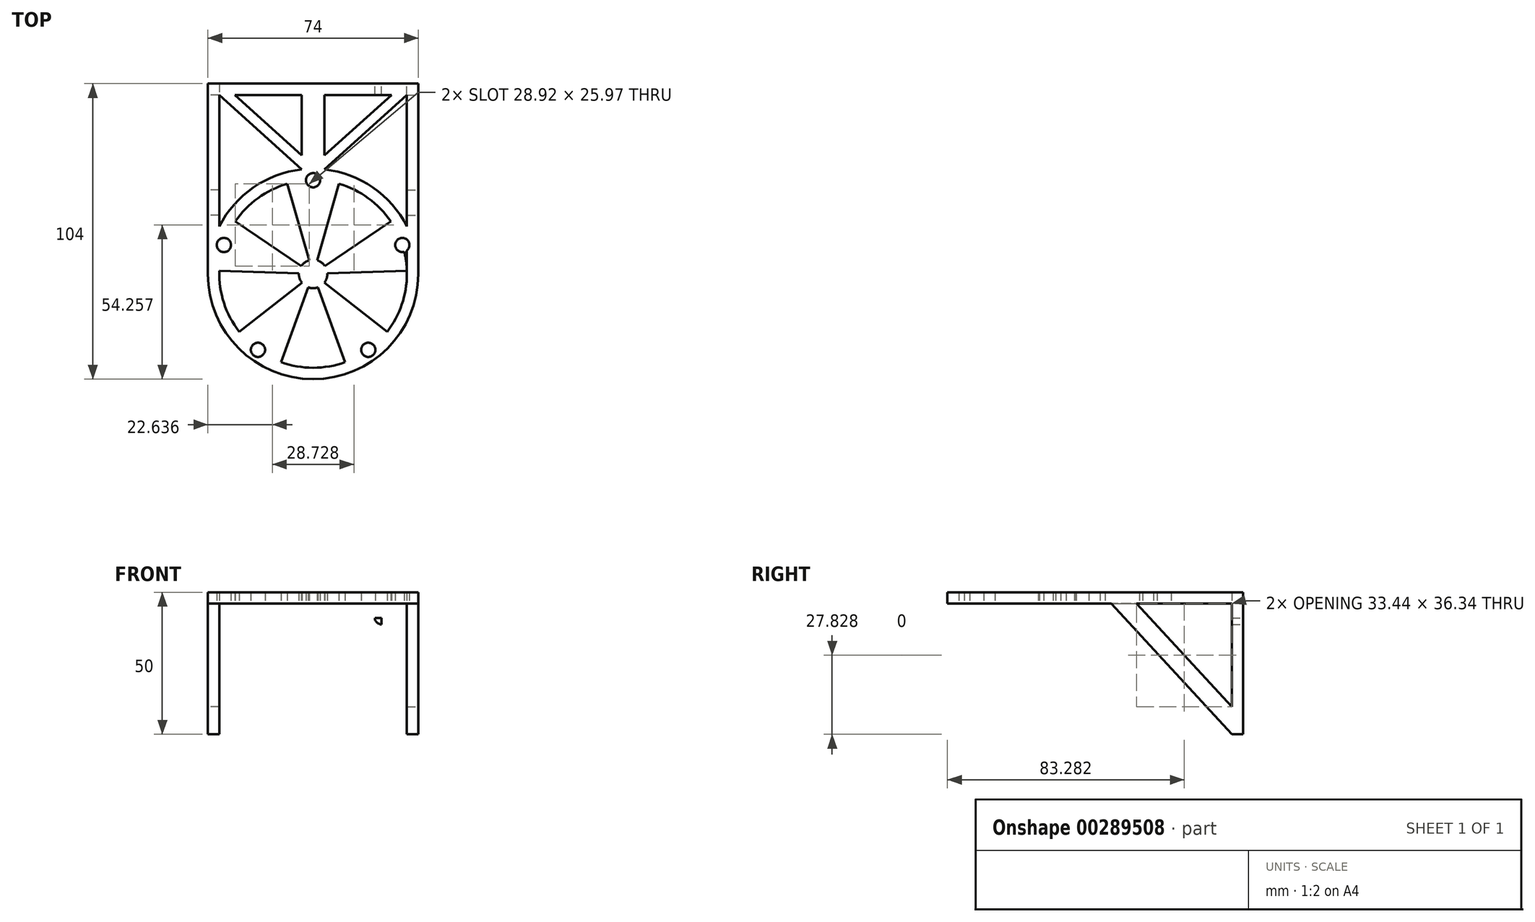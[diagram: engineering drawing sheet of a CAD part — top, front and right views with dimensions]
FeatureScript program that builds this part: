
annotation { "Feature Type Name" : "Feature", "Feature Type Description" : "" }
export const myFeature = defineFeature(function(context is Context, id is Id, definition is map)
    precondition{}
    {
        {
            var Q0;
            Q0=qCreatedBy(makeId("Top.planeOp"),FACE);
            var sketch = newSketch(context, id + "F0", { "sketchPlane" : qUnion([Q0])});
            skCircle(sketch, "E0", {"center": v(0, 33) * mm, "radius": 2.5 * mm});
            skCircle(sketch, "E1.1.0", {"center": v(-31.38, 10.2) * mm, "radius": 2.5 * mm});
            skCircle(sketch, "E1.2.0", {"center": v(-19.4, -26.7) * mm, "radius": 2.5 * mm});
            skCircle(sketch, "E1.3.0", {"center": v(19.4, -26.7) * mm, "radius": 2.5 * mm});
            skCircle(sketch, "E1.4.0", {"center": v(31.38, 10.2) * mm, "radius": 2.5 * mm});
            skPoint(sketch, "E1.center", {"position": v(0, 0) * mm});
            skLineSegment(sketch, "E2", {"start": v(0, 67) * mm, "end": v(37, 67) * mm});
            skLineSegment(sketch, "E3", {"start": v(37, 67) * mm, "end": v(-37, 67) * mm});
            skLineSegment(sketch, "E4", {"start": v(-37, 67) * mm, "end": v(-37, 0) * mm});
            skLineSegment(sketch, "E5", {"start": v(37, 67) * mm, "end": v(37, 0) * mm});
            skLineSegment(sketch, "E6", {"start": v(23.54, 15.9) * mm, "end": v(0, 0) * mm});
            skLineSegment(sketch, "E7", {"start": v(23.54, 15.9) * mm, "end": v(27.35, 18.47) * mm});
            skLineSegment(sketch, "E8", {"start": v(7.85, 27.3) * mm, "end": v(0, 0) * mm});
            skLineSegment(sketch, "E9", {"start": v(0, 0) * mm, "end": v(9.12, 31.72) * mm});
            skLineSegment(sketch, "E10.1.0", {"start": v(0, 0) * mm, "end": v(-27.35, 18.47) * mm});
            skLineSegment(sketch, "E10.1.2", {"start": v(-7.85, 27.3) * mm, "end": v(0, 0) * mm});
            skLineSegment(sketch, "E10.1.4", {"start": v(-7.85, 27.3) * mm, "end": v(-9.12, 31.72) * mm});
            skLineSegment(sketch, "E10.2.0", {"start": v(0, 0) * mm, "end": v(-26.02, -20.3) * mm});
            skLineSegment(sketch, "E10.2.2", {"start": v(-28.39, 0.97) * mm, "end": v(0, 0) * mm});
            skLineSegment(sketch, "E10.2.4", {"start": v(-28.39, 0.97) * mm, "end": v(-32.98, 1.13) * mm});
            skLineSegment(sketch, "E10.3.0", {"start": v(0, 0) * mm, "end": v(11.27, -31.02) * mm});
            skLineSegment(sketch, "E10.3.2", {"start": v(-9.7, -26.7) * mm, "end": v(0, 0) * mm});
            skLineSegment(sketch, "E10.3.4", {"start": v(-9.7, -26.7) * mm, "end": v(-11.27, -31.02) * mm});
            skLineSegment(sketch, "E10.4.0", {"start": v(0, 0) * mm, "end": v(32.98, 1.13) * mm});
            skLineSegment(sketch, "E10.4.2", {"start": v(22.4, -17.47) * mm, "end": v(0, 0) * mm});
            skLineSegment(sketch, "E10.4.4", {"start": v(22.4, -17.47) * mm, "end": v(26.02, -20.3) * mm});
            skLineSegment(sketch, "E11.0", {"start": v(-33, 63) * mm, "end": v(-33, 0) * mm});
            skLineSegment(sketch, "E11.1", {"start": v(33, 63) * mm, "end": v(-33, 63) * mm});
            skLineSegment(sketch, "E11.2", {"start": v(33, 63) * mm, "end": v(33, 0) * mm});
            skLineSegment(sketch, "E12", {"start": v(0, 63) * mm, "end": v(4, 63) * mm});
            skLineSegment(sketch, "E13", {"start": v(4, 63) * mm, "end": v(0, 63) * mm});
            skLineSegment(sketch, "E14.bottom", {"start": v(4, 63) * mm, "end": v(-4, 63) * mm});
            skCircle(sketch, "E15", {"center": v(0, 0) * mm, "radius": 37 * mm});
            skCircle(sketch, "E16", {"center": v(0, 0) * mm, "radius": 33 * mm});
            skCircle(sketch, "E17", {"center": v(0, 0) * mm, "radius": 5 * mm});
            skLineSegment(sketch, "E18", {"start": v(4, 63) * mm, "end": v(4, 36.78) * mm});
            skLineSegment(sketch, "E19", {"start": v(-4, 63) * mm, "end": v(-4, 36.78) * mm});
            skLineSegment(sketch, "E20", {"start": v(-4, 36.78) * mm, "end": v(-33, 63) * mm});
            skLineSegment(sketch, "E21", {"start": v(4, 36.78) * mm, "end": v(33, 63) * mm});
            skLineSegment(sketch, "E22", {"start": v(4, 41.7) * mm, "end": v(27.56, 63) * mm});
            skLineSegment(sketch, "E23", {"start": v(4, 41.7) * mm, "end": v(-4, 41.7) * mm});
            skLineSegment(sketch, "E24", {"start": v(-4, 41.7) * mm, "end": v(-27.56, 63) * mm});
            skSolve(sketch);
        }
        {
            var Q0;
            Q0 = qSketchRegion(id + "F0", true);
            var Q1;
            {var subQ4=sQuery(id+"F0.wireOp",EDGE,"E23");Q1=makeQuery(id+"F0.imprint","IMPRINT",FACE,{"disambiguationData":[TD([[makeQuery(id+"F0.imprint","IMPRINT",EDGE,{"derivedFrom":subQ4}),-1.0]])]});}
            var Q2;
            {var subQ5=sQuery(id+"F0.wireOp",EDGE,"E23");Q2=makeQuery(id+"F0.imprint","IMPRINT",FACE,{"disambiguationData":[TD([[makeQuery(id+"F0.imprint","IMPRINT",EDGE,{"derivedFrom":subQ5}),1.0]])]});}
            var Q3;
            {var subQ0=sQuery(id+"F0.wireOp",EDGE,"E21");Q3=makeQuery(id+"F0.imprint","IMPRINT",FACE,{"disambiguationData":[TD([[makeQuery(id+"F0.imprint","IMPRINT",EDGE,{"derivedFrom":subQ0}),1.0]])]});}
            var Q4;
            {var subQ0=sQuery(id+"F0.wireOp",EDGE,"E20");Q4=makeQuery(id+"F0.imprint","IMPRINT",FACE,{"disambiguationData":[TD([[makeQuery(id+"F0.imprint","IMPRINT",EDGE,{"derivedFrom":subQ0}),-1.0]])]});}
            var Q5;
            {var subQ7=sQuery(id+"F0.wireOp",EDGE,"E16");var subQ14=sQuery(id+"F0.wireOp",EDGE,"E0");var subQ15=makeQuery(id+"F0.imprint","INTERSECT",VERTEX,{"disambiguationData":[OD(0.0)],"derivedFrom":[subQ14,subQ7]});Q5=makeQuery(id+"F0.imprint","IMPRINT",FACE,{"disambiguationData":[TD([[makeQuery(id+"F0.imprint","IMPRINT",EDGE,{"disambiguationData":[TD([[subQ15,-1.0]])],"derivedFrom":subQ14}),-1.0]])]});}
            var Q6;
            {var subQ11=sQuery(id+"F0.wireOp",EDGE,"E10.1.4");Q6=makeQuery(id+"F0.imprint","IMPRINT",FACE,{"disambiguationData":[TD([[makeQuery(id+"F0.imprint","IMPRINT",EDGE,{"derivedFrom":subQ11}),-1.0]])]});}
            var Q7;
            {var subQ5=sQuery(id+"F0.wireOp",EDGE,"E7");Q7=makeQuery(id+"F0.imprint","IMPRINT",FACE,{"disambiguationData":[TD([[makeQuery(id+"F0.imprint","IMPRINT",EDGE,{"derivedFrom":subQ5}),-1.0]])]});}
            var Q8;
            {var subQ0=sQuery(id+"F0.wireOp",EDGE,"E10.4.4");Q8=makeQuery(id+"F0.imprint","IMPRINT",FACE,{"disambiguationData":[TD([[makeQuery(id+"F0.imprint","IMPRINT",EDGE,{"derivedFrom":subQ0}),-1.0]])]});}
            var Q9;
            {var subQ0=sQuery(id+"F0.wireOp",EDGE,"E10.3.4");Q9=makeQuery(id+"F0.imprint","IMPRINT",FACE,{"disambiguationData":[TD([[makeQuery(id+"F0.imprint","IMPRINT",EDGE,{"derivedFrom":subQ0}),-1.0]])]});}
            var Q10;
            {var subQ1=sQuery(id+"F0.wireOp",EDGE,"E10.1.0");var subQ3=sQuery(id+"F0.wireOp",EDGE,"E17");var subQ4=makeQuery(id+"F0.imprint","INTERSECT",VERTEX,{"derivedFrom":[subQ1,subQ3]});Q10=makeQuery(id+"F0.imprint","IMPRINT",FACE,{"disambiguationData":[TD([[makeQuery(id+"F0.imprint","IMPRINT",EDGE,{"disambiguationData":[TD([[subQ4,-1.0]])],"derivedFrom":subQ3}),1.0]])]});}
            var Q11;
            {var subQ0=sQuery(id+"F0.wireOp",EDGE,"E10.2.4");Q11=makeQuery(id+"F0.imprint","IMPRINT",FACE,{"disambiguationData":[TD([[makeQuery(id+"F0.imprint","IMPRINT",EDGE,{"derivedFrom":subQ0}),-1.0]])]});}
            var Q12;
            {var subQ1=sQuery(id+"F0.wireOp",EDGE,"E10.2.0");var subQ3=sQuery(id+"F0.wireOp",EDGE,"E17");var subQ4=makeQuery(id+"F0.imprint","INTERSECT",VERTEX,{"derivedFrom":[subQ1,subQ3]});Q12=makeQuery(id+"F0.imprint","IMPRINT",FACE,{"disambiguationData":[TD([[makeQuery(id+"F0.imprint","IMPRINT",EDGE,{"disambiguationData":[TD([[subQ4,1.0]])],"derivedFrom":subQ3}),1.0]])]});}
            var Q13;
            {var subQ1=sQuery(id+"F0.wireOp",EDGE,"E10.2.0");var subQ3=sQuery(id+"F0.wireOp",EDGE,"E17");var subQ4=makeQuery(id+"F0.imprint","INTERSECT",VERTEX,{"derivedFrom":[subQ1,subQ3]});Q13=makeQuery(id+"F0.imprint","IMPRINT",FACE,{"disambiguationData":[TD([[makeQuery(id+"F0.imprint","IMPRINT",EDGE,{"disambiguationData":[TD([[subQ4,-1.0]])],"derivedFrom":subQ3}),1.0]])]});}
            var Q14;
            {var subQ1=sQuery(id+"F0.wireOp",EDGE,"E10.3.0");var subQ3=sQuery(id+"F0.wireOp",EDGE,"E17");var subQ4=makeQuery(id+"F0.imprint","INTERSECT",VERTEX,{"derivedFrom":[subQ1,subQ3]});Q14=makeQuery(id+"F0.imprint","IMPRINT",FACE,{"disambiguationData":[TD([[makeQuery(id+"F0.imprint","IMPRINT",EDGE,{"disambiguationData":[TD([[subQ4,1.0]])],"derivedFrom":subQ3}),1.0]])]});}
            var Q15;
            {var subQ1=sQuery(id+"F0.wireOp",EDGE,"E10.3.0");var subQ3=sQuery(id+"F0.wireOp",EDGE,"E17");var subQ4=makeQuery(id+"F0.imprint","INTERSECT",VERTEX,{"derivedFrom":[subQ1,subQ3]});Q15=makeQuery(id+"F0.imprint","IMPRINT",FACE,{"disambiguationData":[TD([[makeQuery(id+"F0.imprint","IMPRINT",EDGE,{"disambiguationData":[TD([[subQ4,-1.0]])],"derivedFrom":subQ3}),1.0]])]});}
            var Q16;
            {var subQ1=sQuery(id+"F0.wireOp",EDGE,"E10.4.0");var subQ3=sQuery(id+"F0.wireOp",EDGE,"E17");var subQ4=makeQuery(id+"F0.imprint","INTERSECT",VERTEX,{"derivedFrom":[subQ1,subQ3]});Q16=makeQuery(id+"F0.imprint","IMPRINT",FACE,{"disambiguationData":[TD([[makeQuery(id+"F0.imprint","IMPRINT",EDGE,{"disambiguationData":[TD([[subQ4,1.0]])],"derivedFrom":subQ3}),1.0]])]});}
            var Q17;
            {var subQ1=sQuery(id+"F0.wireOp",EDGE,"E6");var subQ3=sQuery(id+"F0.wireOp",EDGE,"E17");var subQ4=makeQuery(id+"F0.imprint","INTERSECT",VERTEX,{"derivedFrom":[subQ1,subQ3]});Q17=makeQuery(id+"F0.imprint","IMPRINT",FACE,{"disambiguationData":[TD([[makeQuery(id+"F0.imprint","IMPRINT",EDGE,{"disambiguationData":[TD([[subQ4,1.0]])],"derivedFrom":subQ3}),1.0]])]});}
            var Q18;
            {var subQ1=sQuery(id+"F0.wireOp",EDGE,"E6");var subQ3=sQuery(id+"F0.wireOp",EDGE,"E17");var subQ4=makeQuery(id+"F0.imprint","INTERSECT",VERTEX,{"derivedFrom":[subQ1,subQ3]});Q18=makeQuery(id+"F0.imprint","IMPRINT",FACE,{"disambiguationData":[TD([[makeQuery(id+"F0.imprint","IMPRINT",EDGE,{"disambiguationData":[TD([[subQ4,-1.0]])],"derivedFrom":subQ3}),1.0]])]});}
            var Q19;
            {var subQ1=sQuery(id+"F0.wireOp",EDGE,"E9");var subQ3=sQuery(id+"F0.wireOp",EDGE,"E17");var subQ4=makeQuery(id+"F0.imprint","INTERSECT",VERTEX,{"derivedFrom":[subQ1,subQ3]});Q19=makeQuery(id+"F0.imprint","IMPRINT",FACE,{"disambiguationData":[TD([[makeQuery(id+"F0.imprint","IMPRINT",EDGE,{"disambiguationData":[TD([[subQ4,-1.0]])],"derivedFrom":subQ3}),1.0]])]});}
            var Q20;
            {var subQ1=sQuery(id+"F0.wireOp",EDGE,"E10.1.0");var subQ3=sQuery(id+"F0.wireOp",EDGE,"E17");var subQ4=makeQuery(id+"F0.imprint","INTERSECT",VERTEX,{"derivedFrom":[subQ1,subQ3]});Q20=makeQuery(id+"F0.imprint","IMPRINT",FACE,{"disambiguationData":[TD([[makeQuery(id+"F0.imprint","IMPRINT",EDGE,{"disambiguationData":[TD([[subQ4,1.0]])],"derivedFrom":subQ3}),1.0]])]});}
            var Q21;
            {var subQ0=sQuery(id+"F0.wireOp",EDGE,"E11.0");var subQ1=sQuery(id+"F0.wireOp",EDGE,"E1.1.0");var subQ2=makeQuery(id+"F0.imprint","INTERSECT",VERTEX,{"disambiguationData":[OD(0.0)],"derivedFrom":[subQ1,subQ0]});Q21=makeQuery(id+"F0.imprint","IMPRINT",FACE,{"disambiguationData":[TD([[makeQuery(id+"F0.imprint","IMPRINT",EDGE,{"disambiguationData":[TD([[subQ2,-1.0]])],"derivedFrom":subQ1}),-1.0]])]});}
            var Q22;
            {var subQ0=sQuery(id+"F0.wireOp",EDGE,"E11.2");var subQ1=sQuery(id+"F0.wireOp",EDGE,"E1.4.0");var subQ2=makeQuery(id+"F0.imprint","INTERSECT",VERTEX,{"disambiguationData":[OD(1.0)],"derivedFrom":[subQ1,subQ0]});Q22=makeQuery(id+"F0.imprint","IMPRINT",FACE,{"disambiguationData":[TD([[makeQuery(id+"F0.imprint","IMPRINT",EDGE,{"disambiguationData":[TD([[subQ2,1.0]])],"derivedFrom":subQ1}),-1.0]])]});}
            extrude(context, id + "F1", {"entities" : qUnion([Q0, Q1, Q2, Q3, Q4, Q5, Q6, Q7, Q8, Q9, Q10, Q11, Q12, Q13, Q14, Q15, Q16, Q17, Q18, Q19, Q20, Q21, Q22]), "depth" : 4 * mm});
        }
        {
            var Q0;
            Q0=makeQuery(id+"F1.opExtrude","SWEPT_FACE",FACE,{"disambiguationData":[OSD([sQuery(id+"F0.wireOp",EDGE,"E4")])]});
            var sketch = newSketch(context, id + "F2", { "sketchPlane" : qUnion([Q0])});
            skLineSegment(sketch, "E25.bottom", {"start": v(-67, 4) * mm, "end": v(-17, 4) * mm});
            skLineSegment(sketch, "E25.top", {"start": v(-67, -46) * mm, "end": v(-17, -46) * mm});
            skLineSegment(sketch, "E25.left", {"start": v(-67, 4) * mm, "end": v(-67, -46) * mm});
            skLineSegment(sketch, "E25.right", {"start": v(-17, 4) * mm, "end": v(-17, -46) * mm});
            skLineSegment(sketch, "E26.0", {"start": v(-63, 0) * mm, "end": v(-29.56, 0) * mm});
            skLineSegment(sketch, "E26.1", {"start": v(-63, 0) * mm, "end": v(-63, -36.34) * mm});
            skLineSegment(sketch, "E26.2", {"start": v(-63, -36.34) * mm, "end": v(-29.56, 0) * mm});
            skLineSegment(sketch, "E27", {"start": v(-63, -36.34) * mm, "end": v(-63, -46) * mm});
            skLineSegment(sketch, "E28", {"start": v(-63, -46) * mm, "end": v(-17, 4) * mm});
            skSolve(sketch);
        }
        {
            var Q0;
            {var subQ1=sQuery(id+"F2.wireOp",EDGE,"E25.right");var subQ2=sQuery(id+"F0.wireOp",EDGE,"E4");var subQ4=makeQuery(id+"F1.opExtrude","CAP_EDGE",EDGE,{"disambiguationData":[OSD([subQ2])],"isStart":true});var subQ5=makeQuery(id+"F2.imprint","INTERSECT",VERTEX,{"derivedFrom":[subQ4,subQ1]});Q0=makeQuery(id+"F2.imprint","IMPRINT",FACE,{"disambiguationData":[TD([[makeQuery(id+"F2.imprint","IMPRINT",EDGE,{"disambiguationData":[TD([[subQ5,1.0]])],"derivedFrom":subQ4}),1.0]])]});}
            var Q1;
            {var subQ1=sQuery(id+"F2.wireOp",EDGE,"E25.bottom");Q1=makeQuery(id+"F2.imprint","IMPRINT",FACE,{"disambiguationData":[TD([[makeQuery(id+"F2.imprint","IMPRINT",EDGE,{"derivedFrom":subQ1}),-1.0]])]});}
            var Q2;
            {var subQ1=sQuery(id+"F2.wireOp",EDGE,"E26.1");Q2=makeQuery(id+"F2.imprint","IMPRINT",FACE,{"disambiguationData":[TD([[makeQuery(id+"F2.imprint","IMPRINT",EDGE,{"derivedFrom":subQ1}),-1.0]])]});}
            var Q3;
            {var subQ0=sQuery(id+"F2.wireOp",EDGE,"E26.2");Q3=makeQuery(id+"F2.imprint","IMPRINT",FACE,{"disambiguationData":[TD([[makeQuery(id+"F2.imprint","IMPRINT",EDGE,{"derivedFrom":subQ0}),-1.0]])]});}
            extrude(context, id + "F3", {"entities" : qUnion([Q0, Q1, Q2, Q3]), "operationType" : NewBodyOperationType.ADD, "oppositeDirection" : true, "depth" : 4 * mm});
        }
        {
            var Q0;
            Q0=makeQuery(id+"F1.opExtrude","SWEPT_FACE",FACE,{"disambiguationData":[OSD([sQuery(id+"F0.wireOp",EDGE,"E5")])]});
            var sketch = newSketch(context, id + "F4", { "sketchPlane" : qUnion([Q0])});
            skLineSegment(sketch, "E29.bottom", {"start": v(67, 4) * mm, "end": v(17, 4) * mm});
            skLineSegment(sketch, "E29.top", {"start": v(67, -46) * mm, "end": v(17, -46) * mm});
            skLineSegment(sketch, "E29.left", {"start": v(67, 4) * mm, "end": v(67, -46) * mm});
            skLineSegment(sketch, "E29.right", {"start": v(17, 4) * mm, "end": v(17, -46) * mm});
            skLineSegment(sketch, "E30.0", {"start": v(63, 0) * mm, "end": v(26.66, 0) * mm});
            skLineSegment(sketch, "E30.1", {"start": v(63, 0) * mm, "end": v(63, -36.34) * mm});
            skLineSegment(sketch, "E31", {"start": v(63, -46) * mm, "end": v(17, 4) * mm});
            skLineSegment(sketch, "E32", {"start": v(63, -36.34) * mm, "end": v(29.56, 0) * mm});
            skSolve(sketch);
        }
        {
            var Q0;
            {var subQ1=sQuery(id+"F4.wireOp",EDGE,"E29.right");var subQ2=sQuery(id+"F0.wireOp",EDGE,"E5");var subQ4=makeQuery(id+"F1.opExtrude","CAP_EDGE",EDGE,{"disambiguationData":[OSD([subQ2])],"isStart":true});var subQ5=makeQuery(id+"F4.imprint","INTERSECT",VERTEX,{"derivedFrom":[subQ4,subQ1]});Q0=makeQuery(id+"F4.imprint","IMPRINT",FACE,{"disambiguationData":[TD([[makeQuery(id+"F4.imprint","IMPRINT",EDGE,{"disambiguationData":[TD([[subQ5,1.0]])],"derivedFrom":subQ4}),-1.0]])]});}
            var Q1;
            {var subQ1=sQuery(id+"F4.wireOp",EDGE,"E29.bottom");Q1=makeQuery(id+"F4.imprint","IMPRINT",FACE,{"disambiguationData":[TD([[makeQuery(id+"F4.imprint","IMPRINT",EDGE,{"derivedFrom":subQ1}),1.0]])]});}
            var Q2;
            {var subQ1=sQuery(id+"F4.wireOp",EDGE,"E30.1");Q2=makeQuery(id+"F4.imprint","IMPRINT",FACE,{"disambiguationData":[TD([[makeQuery(id+"F4.imprint","IMPRINT",EDGE,{"derivedFrom":subQ1}),1.0]])]});}
            extrude(context, id + "F5", {"entities" : qUnion([Q0, Q1, Q2]), "operationType" : NewBodyOperationType.ADD, "oppositeDirection" : true, "depth" : 4 * mm});
        }
        {
            var Q0;
            Q0=makeQuery(id+"F5.boolean.opBoolean","MERGE",FACE,{"derivedFrom":[makeQuery(id+"F3.boolean.opBoolean","MERGE",FACE,{"derivedFrom":[makeQuery(id+"F1.opExtrude","SWEPT_FACE",FACE,{"disambiguationData":[OSD([sQuery(id+"F0.wireOp",EDGE,"E3")])]}),makeQuery(id+"F3.opExtrude","SWEPT_FACE",FACE,{"disambiguationData":[OSD([sQuery(id+"F2.wireOp",EDGE,"E25.left")])]})]}),makeQuery(id+"F5.opExtrude","SWEPT_FACE",FACE,{"disambiguationData":[OSD([sQuery(id+"F4.wireOp",EDGE,"E29.left")])]})]});
            var sketch = newSketch(context, id + "F6", { "sketchPlane" : qUnion([Q0])});
            skLineSegment(sketch, "E33.bottom", {"start": v(-37, -46) * mm, "end": v(37, -46) * mm});
            skLineSegment(sketch, "E33.top", {"start": v(-37, -36) * mm, "end": v(37, -36) * mm});
            skLineSegment(sketch, "E33.left", {"start": v(-37, -46) * mm, "end": v(-37, -36) * mm});
            skLineSegment(sketch, "E33.right", {"start": v(37, -46) * mm, "end": v(37, -36) * mm});
            skLineSegment(sketch, "E34", {"start": v(-37, -36) * mm, "end": v(-37, 0) * mm});
            skLineSegment(sketch, "E35.bottom", {"start": v(-37, 0) * mm, "end": v(37, 0) * mm});
            skLineSegment(sketch, "E35.top", {"start": v(-37, -10) * mm, "end": v(37, -10) * mm});
            skLineSegment(sketch, "E35.left", {"start": v(-37, 0) * mm, "end": v(-37, -10) * mm});
            skLineSegment(sketch, "E35.right", {"start": v(37, 0) * mm, "end": v(37, -10) * mm});
            skLineSegment(sketch, "E36", {"start": v(0, 0) * mm, "end": v(0, -46) * mm});
            skLineSegment(sketch, "E37.bottom", {"start": v(0, 0) * mm, "end": v(0, 0) * mm});
            skLineSegment(sketch, "E37.top", {"start": v(0, -10) * mm, "end": v(0, -10) * mm});
            skLineSegment(sketch, "E37.left", {"start": v(0, 0) * mm, "end": v(0, -10) * mm});
            skLineSegment(sketch, "E37.right", {"start": v(0, 0) * mm, "end": v(0, -10) * mm});
            skPoint(sketch, "E38.oppositeSnap0", {"position": v(0, -5) * mm});
            skLineSegment(sketch, "E38.bottom", {"start": v(0, -5) * mm, "end": v(24, -5) * mm});
            skLineSegment(sketch, "E38.top", {"start": v(0, -5) * mm, "end": v(24, -5) * mm});
            skLineSegment(sketch, "E38.left", {"start": v(0, -5) * mm, "end": v(0, -5) * mm});
            skLineSegment(sketch, "E38.right", {"start": v(24, -5) * mm, "end": v(24, -5) * mm});
            skLineSegment(sketch, "E39", {"start": v(0, -46) * mm, "end": v(0, -36) * mm});
            skLineSegment(sketch, "E40", {"start": v(0, -36) * mm, "end": v(0, -41) * mm});
            skLineSegment(sketch, "E41", {"start": v(0, -41) * mm, "end": v(-24, -41) * mm});
            skLineSegment(sketch, "E42.bottom", {"start": v(24, -5) * mm, "end": v(-24, -5) * mm});
            skLineSegment(sketch, "E42.top", {"start": v(24, -41) * mm, "end": v(-24, -41) * mm});
            skLineSegment(sketch, "E42.left", {"start": v(24, -5) * mm, "end": v(24, -41) * mm});
            skLineSegment(sketch, "E42.right", {"start": v(-24, -5) * mm, "end": v(-24, -41) * mm});
            skCircle(sketch, "E43", {"center": v(-24, -5) * mm, "radius": 2.3 * mm});
            skCircle(sketch, "E44", {"center": v(24, -5) * mm, "radius": 2.3 * mm});
            skCircle(sketch, "E45", {"center": v(24, -41) * mm, "radius": 2.3 * mm});
            skCircle(sketch, "E46", {"center": v(-24, -41) * mm, "radius": 2.3 * mm});
            skSolve(sketch);
        }
        {
            var Q0;
            {var subQ7=sQuery(id+"F6.wireOp",EDGE,"E40");Q0=makeQuery(id+"F6.imprint","IMPRINT",FACE,{"disambiguationData":[TD([[makeQuery(id+"F6.imprint","IMPRINT",EDGE,{"derivedFrom":subQ7}),1.0]])]});}
            var Q1;
            {var subQ5=sQuery(id+"F6.wireOp",EDGE,"E42.bottom");var subQ7=sQuery(id+"F6.wireOp",EDGE,"E37.right");var subQ8=makeQuery(id+"F6.imprint","INTERSECT",VERTEX,{"derivedFrom":[subQ7,subQ5]});Q1=makeQuery(id+"F6.imprint","IMPRINT",FACE,{"disambiguationData":[TD([[makeQuery(id+"F6.imprint","IMPRINT",EDGE,{"disambiguationData":[TD([[subQ8,1.0]])],"derivedFrom":subQ5}),1.0]])]});}
            var Q2;
            {var subQ0=sQuery(id+"F6.wireOp",EDGE,"E33.right");Q2=makeQuery(id+"F6.imprint","IMPRINT",FACE,{"disambiguationData":[TD([[makeQuery(id+"F6.imprint","IMPRINT",EDGE,{"derivedFrom":subQ0}),-1.0]])]});}
            var Q3;
            {var subQ0=sQuery(id+"F6.wireOp",EDGE,"E34");Q3=makeQuery(id+"F6.imprint","IMPRINT",FACE,{"disambiguationData":[TD([[makeQuery(id+"F6.imprint","IMPRINT",EDGE,{"derivedFrom":subQ0}),1.0]])]});}
            var Q4;
            {var subQ1=sQuery(id+"F6.wireOp",EDGE,"E39");Q4=makeQuery(id+"F6.imprint","IMPRINT",FACE,{"disambiguationData":[TD([[makeQuery(id+"F6.imprint","IMPRINT",EDGE,{"derivedFrom":subQ1}),-1.0]])]});}
            var Q5;
            {var subQ5=sQuery(id+"F6.wireOp",EDGE,"E35.bottom");var subQ7=makeQuery(id+"F3.opExtrude","CAP_EDGE",EDGE,{"disambiguationData":[OSD([sQuery(id+"F2.wireOp",EDGE,"E25.left")])],"isStart":false});var subQ8=makeQuery(id+"F6.imprint","INTERSECT",VERTEX,{"derivedFrom":[subQ7,subQ5]});Q5=makeQuery(id+"F6.imprint","IMPRINT",FACE,{"disambiguationData":[TD([[makeQuery(id+"F6.imprint","IMPRINT",EDGE,{"disambiguationData":[TD([[subQ8,1.0]])],"derivedFrom":subQ5}),-1.0]])]});}
            var Q6;
            {var subQ3=sQuery(id+"F0.wireOp",EDGE,"E3");var subQ9=makeQuery(id+"F1.opExtrude","CAP_EDGE",EDGE,{"disambiguationData":[OSD([subQ3])],"isStart":false});Q6=makeQuery(id+"F6.imprint","IMPRINT",FACE,{"disambiguationData":[TD([[makeQuery(id+"F6.imprint","IMPRINT",EDGE,{"derivedFrom":subQ9}),-1.0]])]});}
            var Q7;
            {var subQ5=sQuery(id+"F6.wireOp",EDGE,"E35.bottom");var subQ11=makeQuery(id+"F5.opExtrude","CAP_EDGE",EDGE,{"disambiguationData":[OSD([sQuery(id+"F4.wireOp",EDGE,"E29.left")])],"isStart":false});var subQ13=makeQuery(id+"F6.imprint","INTERSECT",VERTEX,{"derivedFrom":[subQ11,subQ5]});Q7=makeQuery(id+"F6.imprint","IMPRINT",FACE,{"disambiguationData":[TD([[makeQuery(id+"F6.imprint","IMPRINT",EDGE,{"disambiguationData":[TD([[subQ13,-1.0]])],"derivedFrom":subQ5}),-1.0]])]});}
            var Q8;
            {var subQ0=sQuery(id+"F6.wireOp",EDGE,"E42.bottom");var subQ1=sQuery(id+"F6.wireOp",EDGE,"E37.right");var subQ2=makeQuery(id+"F6.imprint","INTERSECT",VERTEX,{"derivedFrom":[subQ1,subQ0]});Q8=makeQuery(id+"F6.imprint","IMPRINT",FACE,{"disambiguationData":[TD([[makeQuery(id+"F6.imprint","IMPRINT",EDGE,{"disambiguationData":[TD([[subQ2,-1.0]])],"derivedFrom":subQ0}),1.0]])]});}
            var Q9;
            {var subQ0=sQuery(id+"F6.wireOp",EDGE,"E40");Q9=makeQuery(id+"F6.imprint","IMPRINT",FACE,{"disambiguationData":[TD([[makeQuery(id+"F6.imprint","IMPRINT",EDGE,{"derivedFrom":subQ0}),-1.0]])]});}
            var Q10;
            {var subQ1=sQuery(id+"F6.wireOp",EDGE,"E39");Q10=makeQuery(id+"F6.imprint","IMPRINT",FACE,{"disambiguationData":[TD([[makeQuery(id+"F6.imprint","IMPRINT",EDGE,{"derivedFrom":subQ1}),1.0]])]});}
            extrude(context, id + "F7", {"entities" : qUnion([Q0, Q1, Q2, Q3, Q4, Q5, Q6, Q7, Q8, Q9, Q10]), "operationType" : NewBodyOperationType.ADD, "oppositeDirection" : true, "depth" : 4 * mm});
        }
    });
